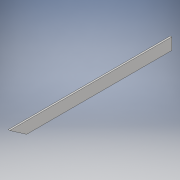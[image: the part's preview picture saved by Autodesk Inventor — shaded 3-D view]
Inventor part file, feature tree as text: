
AUTODESK INVENTOR PART (.ipt)
format: ipt  version: 2019 (Build 230136000, 136)  size: 96,256 bytes
history: native  units: in
note: dims shown in document units (in); Inventor stores cm internally (conversion verified against a paired STEP export)
features: extrude x1, sketch x1
ambient origin geometry x8: Origin, YZ Plane, XZ Plane, XY Plane, X Axis, Y Axis, Z Axis, Center Point
bodies: Solid1 (feature_tree)
feature tree (2):
  extrude  "Extrusion1"  Depth=0.875in
  sketch  "Sketch1"  dims[d0=12.0866in d1=0.875in d2=10.8268in d3=0.1181in d4=0.0in]
